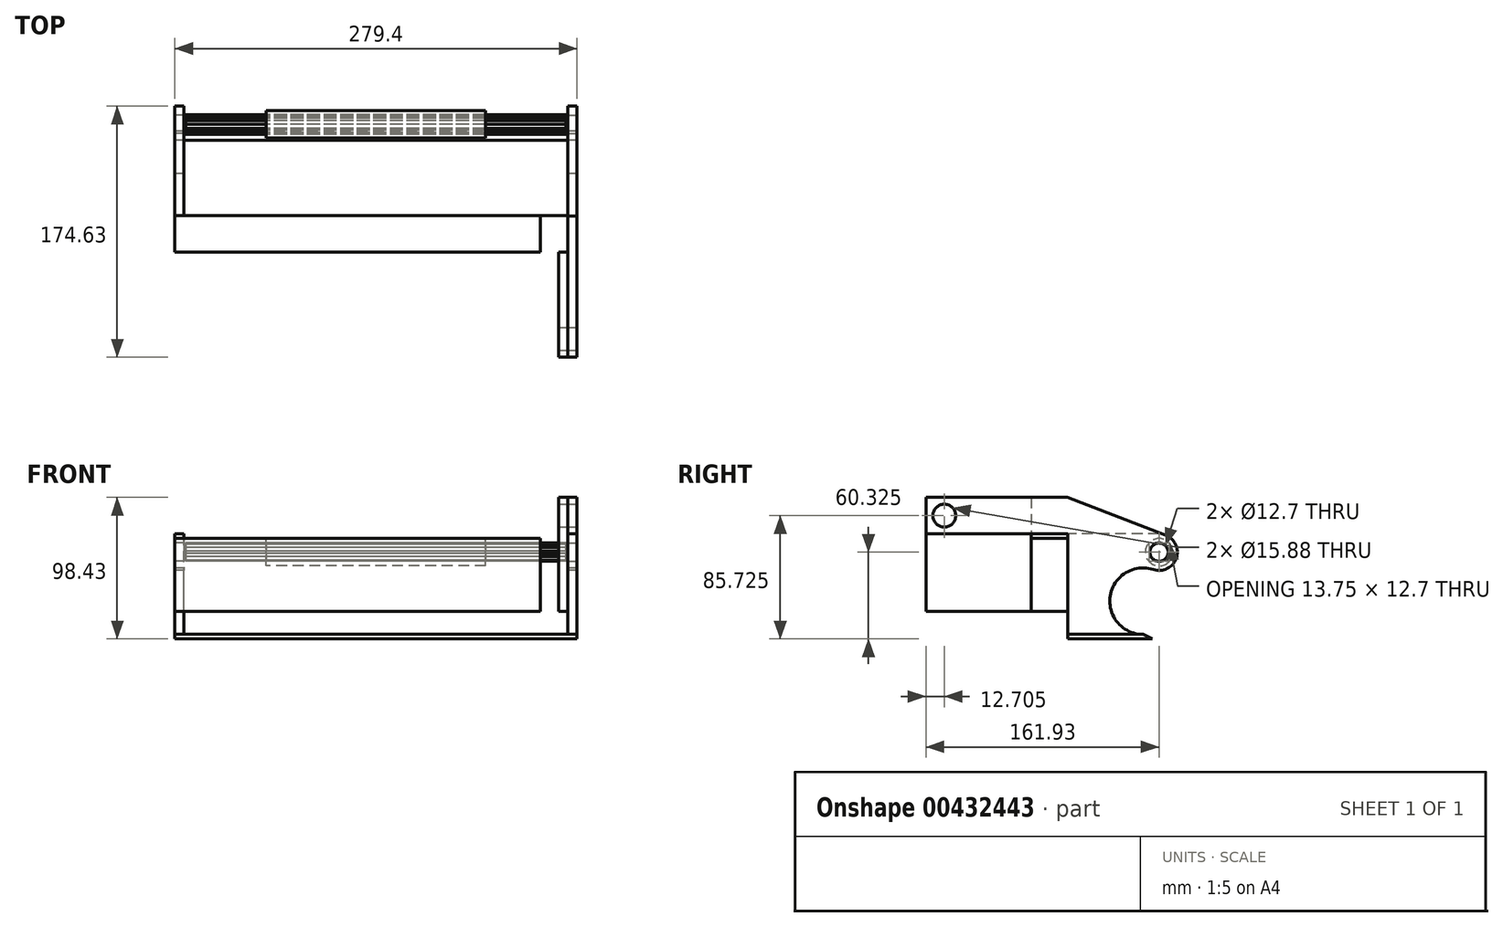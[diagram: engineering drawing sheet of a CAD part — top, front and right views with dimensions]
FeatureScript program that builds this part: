
annotation { "Feature Type Name" : "Feature", "Feature Type Description" : "" }
export const myFeature = defineFeature(function(context is Context, id is Id, definition is map)
    precondition{}
    {
        {
            var Q0;
            Q0=qCreatedBy(makeId("Right.planeOp"),FACE);
            var sketch = newSketch(context, id + "F0", { "sketchPlane" : qUnion([Q0])});
            skLineSegment(sketch, "E0.bottom", {"start": v(0, 19.05) * mm, "end": v(25.4, 19.05) * mm});
            skLineSegment(sketch, "E0.top", {"start": v(0, 69.85) * mm, "end": v(25.4, 69.85) * mm});
            skLineSegment(sketch, "E0.left", {"start": v(0, 19.05) * mm, "end": v(0, 69.85) * mm});
            skLineSegment(sketch, "E0.right", {"start": v(25.4, 19.05) * mm, "end": v(25.4, 69.85) * mm});
            skSolve(sketch);
        }
        {
            var Q0;
            Q0 = qSketchRegion(id + "F0", true);
            extrude(context, id + "F1", {"entities" : qUnion([Q0]), "depth" : 254 * mm});
        }
        {
            var Q0;
            Q0=qCreatedBy(makeId("Right.planeOp"),FACE);
            var sketch = newSketch(context, id + "F2", { "sketchPlane" : qUnion([Q0])});
            skLineSegment(sketch, "E1.bottom", {"start": v(25.4, 0) * mm, "end": v(84.14, 0) * mm});
            skLineSegment(sketch, "E1.top", {"start": v(25.4, 3.18) * mm, "end": v(77.79, 3.18) * mm});
            skLineSegment(sketch, "E1.left", {"start": v(25.4, 0) * mm, "end": v(25.4, 3.18) * mm});
            skLineSegment(sketch, "E2", {"start": v(84.14, 0) * mm, "end": v(77.79, 3.18) * mm});
            skSolve(sketch);
        }
        {
            var Q0;
            Q0 = qSketchRegion(id + "F2", true);
            extrude(context, id + "F3", {"entities" : qUnion([Q0]), "depth" : 279.4 * mm});
        }
        {
            var Q0;
            Q0=makeQuery(id+"F3.opExtrude","CAP_FACE",FACE,{"disambiguationData":[OSD([sQuery(id+"F2.wireOp",EDGE,"E1.bottom"),sQuery(id+"F2.wireOp",EDGE,"E1.top"),sQuery(id+"F2.wireOp",EDGE,"E1.left"),sQuery(id+"F2.wireOp",EDGE,"E2")])],"isStart":false});
            var Q1;
            Q1=makeQuery(id+"F3.opExtrude","CAP_FACE",FACE,{"disambiguationData":[OSD([sQuery(id+"F2.wireOp",EDGE,"E1.bottom"),sQuery(id+"F2.wireOp",EDGE,"E1.top"),sQuery(id+"F2.wireOp",EDGE,"E1.left"),sQuery(id+"F2.wireOp",EDGE,"E2")])],"isStart":true});
            cPlane(context, id + "F4", {"entities" : qUnion([Q0, Q1]), "cplaneType" : CPlaneType.MID_PLANE, "offset" : 25.4 * mm, "width" : 152.4 * mm, "height" : 152.4 * mm});
        }
        {
            var Q0;
            Q0=qCreatedBy(id+"F4.planeOp",FACE);
            var sketch = newSketch(context, id + "F5", { "sketchPlane" : qUnion([Q0])});
            skCircle(sketch, "E3.cCircle", {"center": v(88.9, 60.33) * mm, "radius": 6.35 * mm, "construction": true});
            skLineSegment(sketch, "E3.0", {"start": v(96.23, 60.33) * mm, "end": v(92.57, 53.98) * mm});
            skLineSegment(sketch, "E3.1", {"start": v(92.57, 53.98) * mm, "end": v(85.23, 53.98) * mm});
            skLineSegment(sketch, "E3.2", {"start": v(85.23, 53.97) * mm, "end": v(81.57, 60.32) * mm});
            skLineSegment(sketch, "E3.3", {"start": v(81.57, 60.32) * mm, "end": v(85.23, 66.68) * mm});
            skLineSegment(sketch, "E3.4", {"start": v(85.23, 66.68) * mm, "end": v(92.57, 66.68) * mm});
            skLineSegment(sketch, "E3.5", {"start": v(92.57, 66.68) * mm, "end": v(96.23, 60.33) * mm});
            skPoint(sketch, "E3.0.midPoint", {"position": v(94.4, 57.15) * mm});
            skCircle(sketch, "E4", {"center": v(88.9, 60.33) * mm, "radius": 6.88 * mm});
            skCircle(sketch, "E5", {"center": v(88.9, 60.33) * mm, "radius": 2.55 * mm});
            skSolve(sketch);
        }
        {
            var Q0;
            {var subQ0=sQuery(id+"F5.wireOp",EDGE,"E4");var subQ14=sQuery(id+"F5.wireOp",EDGE,"E3.0");var subQ15=makeQuery(id+"F5.imprint","INTERSECT",VERTEX,{"disambiguationData":[OD(0.0)],"derivedFrom":[subQ14,subQ0]});Q0=makeQuery(id+"F5.imprint","IMPRINT",FACE,{"disambiguationData":[TD([[makeQuery(id+"F5.imprint","IMPRINT",EDGE,{"disambiguationData":[TD([[subQ15,-1.0]])],"derivedFrom":subQ14}),-1.0]])]});}
            extrude(context, id + "F6", {"entities" : qUnion([Q0]), "depth" : 264.16 * mm, "symmetric" : true});
        }
        {
            var Q0;
            Q0=qCreatedBy(id+"F4.planeOp",FACE);
            var sketch = newSketch(context, id + "F7", { "sketchPlane" : qUnion([Q0])});
            skLineSegment(sketch, "E6.0.0", {"start": v(93.08, 65.78) * mm, "end": v(95.72, 61.22) * mm});
            skArc(sketch, "E6.0.1", {"start": v(95.72, 61.22) * mm, "mid": v(95.78, 60.33) * mm, "end": v(95.72, 59.43) * mm});
            skLineSegment(sketch, "E6.0.2", {"start": v(95.72, 59.43) * mm, "end": v(93.08, 54.87) * mm});
            skArc(sketch, "E6.0.3", {"start": v(93.08, 54.87) * mm, "mid": v(92.34, 54.37) * mm, "end": v(91.53, 53.97) * mm});
            skLineSegment(sketch, "E6.0.4", {"start": v(91.53, 53.98) * mm, "end": v(86.27, 53.98) * mm});
            skArc(sketch, "E6.0.5", {"start": v(86.27, 53.98) * mm, "mid": v(85.46, 54.37) * mm, "end": v(84.72, 54.87) * mm});
            skLineSegment(sketch, "E6.0.6", {"start": v(84.72, 54.87) * mm, "end": v(82.08, 59.43) * mm});
            skArc(sketch, "E6.0.7", {"start": v(82.08, 59.43) * mm, "mid": v(82.03, 60.32) * mm, "end": v(82.08, 61.22) * mm});
            skLineSegment(sketch, "E6.0.8", {"start": v(82.08, 61.22) * mm, "end": v(84.72, 65.78) * mm});
            skArc(sketch, "E6.0.9", {"start": v(84.72, 65.78) * mm, "mid": v(85.46, 66.28) * mm, "end": v(86.27, 66.68) * mm});
            skLineSegment(sketch, "E6.0.10", {"start": v(86.27, 66.68) * mm, "end": v(91.53, 66.68) * mm});
            skArc(sketch, "E6.0.11", {"start": v(91.53, 66.68) * mm, "mid": v(92.34, 66.28) * mm, "end": v(93.08, 65.78) * mm});
            skCircle(sketch, "E7", {"center": v(88.9, 60.33) * mm, "radius": 9.53 * mm});
            skSolve(sketch);
        }
        {
            var Q0;
            Q0 = qSketchRegion(id + "F7", true);
            extrude(context, id + "F8", {"entities" : qUnion([Q0]), "depth" : 152.4 * mm, "symmetric" : true});
        }
        {
            var Q0;
            Q0=makeQuery(id+"F3.opExtrude","CAP_FACE",FACE,{"disambiguationData":[OSD([sQuery(id+"F2.wireOp",EDGE,"E1.bottom"),sQuery(id+"F2.wireOp",EDGE,"E1.top"),sQuery(id+"F2.wireOp",EDGE,"E1.left"),sQuery(id+"F2.wireOp",EDGE,"E2")])],"isStart":true});
            var sketch = newSketch(context, id + "F9", { "sketchPlane" : qUnion([Q0])});
            skLineSegment(sketch, "E8.bottom", {"start": v(-101.6, 3.17) * mm, "end": v(-25.4, 3.17) * mm});
            skLineSegment(sketch, "E8.top", {"start": v(-101.6, 73.03) * mm, "end": v(-25.4, 73.03) * mm});
            skLineSegment(sketch, "E8.left", {"start": v(-101.6, 3.18) * mm, "end": v(-101.6, 73.03) * mm});
            skLineSegment(sketch, "E8.right", {"start": v(-25.4, 3.18) * mm, "end": v(-25.4, 73.03) * mm});
            skSolve(sketch);
        }
        {
            var Q0;
            Q0 = qSketchRegion(id + "F9", true);
            extrude(context, id + "F10", {"entities" : qUnion([Q0]), "oppositeDirection" : true, "depth" : 6.35 * mm});
        }
        {
            var Q0;
            Q0=makeQuery(id+"F10.opExtrude","CAP_FACE",FACE,{"disambiguationData":[OSD([sQuery(id+"F9.wireOp",EDGE,"E8.bottom"),sQuery(id+"F9.wireOp",EDGE,"E8.top"),sQuery(id+"F9.wireOp",EDGE,"E8.left"),sQuery(id+"F9.wireOp",EDGE,"E8.right")])],"isStart":true});
            var sketch = newSketch(context, id + "F11", { "sketchPlane" : qUnion([Q0])});
            skCircle(sketch, "E9", {"center": v(-88.9, 60.33) * mm, "radius": 6.35 * mm});
            skLineSegment(sketch, "E10.0.0", {"start": v(-93.08, 65.78) * mm, "end": v(-95.72, 61.22) * mm, "construction": true});
            skArc(sketch, "E10.0.1", {"start": v(-95.72, 61.22) * mm, "mid": v(-95.78, 60.33) * mm, "end": v(-95.72, 59.43) * mm, "construction": true});
            skLineSegment(sketch, "E10.0.2", {"start": v(-95.72, 59.43) * mm, "end": v(-93.08, 54.87) * mm, "construction": true});
            skArc(sketch, "E10.0.3", {"start": v(-93.08, 54.87) * mm, "mid": v(-92.34, 54.37) * mm, "end": v(-91.53, 53.97) * mm, "construction": true});
            skLineSegment(sketch, "E10.0.4", {"start": v(-91.53, 53.98) * mm, "end": v(-86.27, 53.98) * mm, "construction": true});
            skArc(sketch, "E10.0.5", {"start": v(-86.27, 53.98) * mm, "mid": v(-85.46, 54.37) * mm, "end": v(-84.72, 54.87) * mm, "construction": true});
            skLineSegment(sketch, "E10.0.6", {"start": v(-84.72, 54.87) * mm, "end": v(-82.08, 59.43) * mm, "construction": true});
            skArc(sketch, "E10.0.7", {"start": v(-82.08, 59.43) * mm, "mid": v(-82.03, 60.32) * mm, "end": v(-82.08, 61.22) * mm, "construction": true});
            skLineSegment(sketch, "E10.0.8", {"start": v(-82.08, 61.22) * mm, "end": v(-84.72, 65.78) * mm, "construction": true});
            skArc(sketch, "E10.0.9", {"start": v(-84.72, 65.78) * mm, "mid": v(-85.46, 66.28) * mm, "end": v(-86.27, 66.68) * mm, "construction": true});
            skLineSegment(sketch, "E10.0.10", {"start": v(-86.27, 66.68) * mm, "end": v(-91.53, 66.68) * mm, "construction": true});
            skArc(sketch, "E10.0.11", {"start": v(-91.53, 66.68) * mm, "mid": v(-92.34, 66.28) * mm, "end": v(-93.08, 65.78) * mm, "construction": true});
            skSolve(sketch);
        }
        {
            var Q0;
            Q0 = qSketchRegion(id + "F11", true);
            extrude(context, id + "F12", {"entities" : qUnion([Q0]), "operationType" : NewBodyOperationType.REMOVE, "endBound" : BoundingType.THROUGH_ALL, "oppositeDirection" : true, "depth" : 25.4 * mm});
        }
        {
            var Q0;
            Q0=makeQuery(id+"F6.opExtrude","CAP_FACE",FACE,{"disambiguationData":[OSD([sQuery(id+"F5.wireOp",EDGE,"E3.0"),sQuery(id+"F5.wireOp",EDGE,"E3.1"),sQuery(id+"F5.wireOp",EDGE,"E3.2"),sQuery(id+"F5.wireOp",EDGE,"E3.3"),sQuery(id+"F5.wireOp",EDGE,"E3.4"),sQuery(id+"F5.wireOp",EDGE,"E3.5"),sQuery(id+"F5.wireOp",EDGE,"E4"),sQuery(id+"F5.wireOp",EDGE,"E5")])],"isStart":true});
            var sketch = newSketch(context, id + "F13", { "sketchPlane" : qUnion([Q0])});
            skCircle(sketch, "E11", {"center": v(-88.9, 60.33) * mm, "radius": 3.18 * mm});
            skSolve(sketch);
        }
        {
            var Q0;
            Q0 = qSketchRegion(id + "F13", true);
            extrude(context, id + "F14", {"entities" : qUnion([Q0]), "oppositeDirection" : true, "depth" : 4.76 * mm});
        }
        {
            var Q0;
            Q0=makeQuery(id+"F14.opExtrude","SWEPT_BODY",BODY,{"disambiguationData":[OSD([sQuery(id+"F13.wireOp",EDGE,"E11")])]});
            var Q1;
            Q1=qCreatedBy(id+"F4.planeOp",FACE);
            mirror(context, id + "F15", {"operationType" : NewBodyOperationType.ADD, "entities" : qUnion([Q0]), "mirrorPlane" : qUnion([Q1])});
        }
        {
            var Q0;
            Q0=makeQuery(id+"F15.opPattern","COPY",BODY,{"derivedFrom":makeQuery(id+"F14.opExtrude","SWEPT_BODY",BODY,{"disambiguationData":[OSD([sQuery(id+"F13.wireOp",EDGE,"E11")])]}),"instanceName":"1"});
            var Q1;
            Q1=makeQuery(id+"F14.opExtrude","SWEPT_BODY",BODY,{"disambiguationData":[OSD([sQuery(id+"F13.wireOp",EDGE,"E11")])]});
            var Q2;
            Q2=makeQuery(id+"F6.opExtrude","SWEPT_BODY",BODY,{"disambiguationData":[OSD([sQuery(id+"F5.wireOp",EDGE,"E3.0"),sQuery(id+"F5.wireOp",EDGE,"E3.1"),sQuery(id+"F5.wireOp",EDGE,"E3.2"),sQuery(id+"F5.wireOp",EDGE,"E3.3"),sQuery(id+"F5.wireOp",EDGE,"E3.4"),sQuery(id+"F5.wireOp",EDGE,"E3.5"),sQuery(id+"F5.wireOp",EDGE,"E4"),sQuery(id+"F5.wireOp",EDGE,"E5")])]});
            booleanBodies(context, id + "F16", {"operationType" : BooleanOperationType.SUBTRACTION, "tools" : qUnion([Q0, Q1]), "targets" : qUnion([Q2])});
        }
        {
            var Q0;
            Q0=makeQuery(id+"F10.opExtrude","SWEPT_BODY",BODY,{"disambiguationData":[OSD([sQuery(id+"F9.wireOp",EDGE,"E8.bottom"),sQuery(id+"F9.wireOp",EDGE,"E8.top"),sQuery(id+"F9.wireOp",EDGE,"E8.left"),sQuery(id+"F9.wireOp",EDGE,"E8.right")])]});
            var Q1;
            Q1=qCreatedBy(id+"F4.planeOp",FACE);
            mirror(context, id + "F17", {"entities" : qUnion([Q0]), "mirrorPlane" : qUnion([Q1])});
        }
        {
            var Q0;
            Q0=makeQuery(id+"F10.opExtrude","CAP_FACE",FACE,{"disambiguationData":[OSD([sQuery(id+"F9.wireOp",EDGE,"E8.bottom"),sQuery(id+"F9.wireOp",EDGE,"E8.top"),sQuery(id+"F9.wireOp",EDGE,"E8.left"),sQuery(id+"F9.wireOp",EDGE,"E8.right")])],"isStart":true});
            var sketch = newSketch(context, id + "F18", { "sketchPlane" : qUnion([Q0])});
            skCircle(sketch, "E12", {"center": v(-88.9, 60.33) * mm, "radius": 12.7 * mm});
            skCircle(sketch, "E13", {"center": v(-77.79, 26.28) * mm, "radius": 23.1 * mm});
            skLineSegment(sketch, "E14.0", {"start": v(-25.4, 3.18) * mm, "end": v(-77.79, 3.18) * mm, "construction": true});
            skSolve(sketch);
        }
        {
            var Q0;
            {var subQ0=sQuery(id+"F18.wireOp",EDGE,"E12");var subQ1=makeQuery(id+"F10.opExtrude","CAP_EDGE",EDGE,{"disambiguationData":[OSD([sQuery(id+"F9.wireOp",EDGE,"E8.left")])],"isStart":true});var subQ2=makeQuery(id+"F18.imprint","INTERSECT",VERTEX,{"derivedFrom":[subQ1,subQ0]});Q0=makeQuery(id+"F18.imprint","IMPRINT",FACE,{"disambiguationData":[TD([[makeQuery(id+"F18.imprint","IMPRINT",EDGE,{"disambiguationData":[TD([[subQ2,1.0]])],"derivedFrom":subQ0}),-1.0]])]});}
            var Q1;
            {var subQ0=sQuery(id+"F18.wireOp",EDGE,"E13");var subQ1=sQuery(id+"F18.wireOp",EDGE,"E12");var subQ2=makeQuery(id+"F18.imprint","INTERSECT",VERTEX,{"derivedFrom":[subQ1,subQ0]});Q1=makeQuery(id+"F18.imprint","IMPRINT",FACE,{"disambiguationData":[TD([[makeQuery(id+"F18.imprint","IMPRINT",EDGE,{"disambiguationData":[TD([[subQ2,1.0]])],"derivedFrom":subQ1}),-1.0]])]});}
            var Q2;
            {var subQ0=sQuery(id+"F18.wireOp",EDGE,"E13");var subQ1=makeQuery(id+"F18.imprint","INTERSECT",VERTEX,{"derivedFrom":[sQuery(id+"F18.wireOp",EDGE,"E12"),subQ0]});Q2=makeQuery(id+"F18.imprint","IMPRINT",FACE,{"disambiguationData":[TD([[makeQuery(id+"F18.imprint","IMPRINT",EDGE,{"disambiguationData":[TD([[subQ1,-1.0]])],"derivedFrom":subQ0}),1.0]])]});}
            var Q3;
            {var subQ0=sQuery(id+"F18.wireOp",EDGE,"E13");var subQ1=makeQuery(id+"F10.opExtrude","CAP_EDGE",EDGE,{"disambiguationData":[OSD([sQuery(id+"F9.wireOp",EDGE,"E8.left")])],"isStart":true});var subQ2=makeQuery(id+"F18.imprint","INTERSECT",VERTEX,{"disambiguationData":[OD(1.0)],"derivedFrom":[subQ1,subQ0]});Q3=makeQuery(id+"F18.imprint","IMPRINT",FACE,{"disambiguationData":[TD([[makeQuery(id+"F18.imprint","IMPRINT",EDGE,{"disambiguationData":[TD([[subQ2,-1.0]])],"derivedFrom":subQ0}),-1.0]])]});}
            extrude(context, id + "F19", {"entities" : qUnion([Q0, Q1, Q2, Q3]), "operationType" : NewBodyOperationType.REMOVE, "endBound" : BoundingType.THROUGH_ALL, "oppositeDirection" : true, "depth" : 25.4 * mm});
        }
        {
            var Q0;
            Q0=makeQuery(id+"F17.opPattern","COPY",FACE,{"derivedFrom":makeQuery(id+"F10.opExtrude","CAP_FACE",FACE,{"disambiguationData":[OSD([sQuery(id+"F9.wireOp",EDGE,"E8.bottom"),sQuery(id+"F9.wireOp",EDGE,"E8.top"),sQuery(id+"F9.wireOp",EDGE,"E8.left"),sQuery(id+"F9.wireOp",EDGE,"E8.right")])],"isStart":true}),"instanceName":"1"});
            var sketch = newSketch(context, id + "F20", { "sketchPlane" : qUnion([Q0])});
            skLineSegment(sketch, "E15.bottom", {"start": v(-73.03, 98.43) * mm, "end": v(101.44, 98.43) * mm});
            skLineSegment(sketch, "E15.top", {"start": v(-73.03, 73.03) * mm, "end": v(101.44, 73.03) * mm});
            skLineSegment(sketch, "E15.left", {"start": v(-73.03, 98.43) * mm, "end": v(-73.03, 73.03) * mm});
            skLineSegment(sketch, "E15.right", {"start": v(101.44, 98.43) * mm, "end": v(101.44, 73.03) * mm});
            skArc(sketch, "E16.0", {"start": v(84.96, 48.25) * mm, "mid": v(101.44, 58.33) * mm, "end": v(88.9, 73.03) * mm});
            skLineSegment(sketch, "E17", {"start": v(101.44, 73.03) * mm, "end": v(101.44, 58.33) * mm});
            skPoint(sketch, "E17.endSnap0", {"position": v(101.44, 58.33) * mm});
            skSolve(sketch);
        }
        {
            var Q0;
            Q0 = qSketchRegion(id + "F20", true);
            var Q1;
            Q1=makeQuery(id+"F17.opPattern","COPY",FACE,{"derivedFrom":makeQuery(id+"F10.opExtrude","CAP_FACE",FACE,{"disambiguationData":[OSD([sQuery(id+"F9.wireOp",EDGE,"E8.bottom"),sQuery(id+"F9.wireOp",EDGE,"E8.top"),sQuery(id+"F9.wireOp",EDGE,"E8.left"),sQuery(id+"F9.wireOp",EDGE,"E8.right")])],"isStart":false}),"instanceName":"1"});
            extrude(context, id + "F21", {"entities" : qUnion([Q0]), "operationType" : NewBodyOperationType.ADD, "endBound" : BoundingType.UP_TO_SURFACE, "oppositeDirection" : true, "endBoundEntityFace" : qUnion([Q1]), "depth" : 25.4 * mm});
        }
        {
            var Q0;
            Q0=makeQuery(id+"F21.boolean.opBoolean","MERGE",FACE,{"derivedFrom":[makeQuery(id+"F17.opPattern","COPY",FACE,{"derivedFrom":makeQuery(id+"F10.opExtrude","CAP_FACE",FACE,{"disambiguationData":[OSD([sQuery(id+"F9.wireOp",EDGE,"E8.bottom"),sQuery(id+"F9.wireOp",EDGE,"E8.top"),sQuery(id+"F9.wireOp",EDGE,"E8.left"),sQuery(id+"F9.wireOp",EDGE,"E8.right")])],"isStart":true}),"instanceName":"1"}),makeQuery(id+"F21.opExtrude","CAP_FACE",FACE,{"disambiguationData":[OSD([sQuery(id+"F20.wireOp",EDGE,"E15.bottom"),sQuery(id+"F20.wireOp",EDGE,"E15.top"),sQuery(id+"F20.wireOp",EDGE,"E15.left"),sQuery(id+"F20.wireOp",EDGE,"E15.right")])],"isStart":true})]});
            var sketch = newSketch(context, id + "F22", { "sketchPlane" : qUnion([Q0])});
            skCircle(sketch, "E18", {"center": v(-60.33, 85.73) * mm, "radius": 7.94 * mm});
            skLineSegment(sketch, "E19", {"start": v(-73.03, 85.72) * mm, "end": v(-60.33, 85.72) * mm, "construction": true});
            skCircle(sketch, "E20", {"center": v(88.9, 60.33) * mm, "radius": 12.7 * mm});
            skLineSegment(sketch, "E21", {"start": v(93.46, 72.18) * mm, "end": v(25.24, 98.43) * mm});
            skLineSegment(sketch, "E22", {"start": v(25.24, 98.43) * mm, "end": v(101.44, 98.43) * mm});
            skLineSegment(sketch, "E23", {"start": v(101.44, 98.43) * mm, "end": v(101.6, 60.38) * mm});
            skSolve(sketch);
        }
        {
            var Q0;
            Q0=makeQuery(id+"F22.imprint","IMPRINT",FACE,{"disambiguationData":[TD([[makeQuery(id+"F22.imprint","IMPRINT",EDGE,{"derivedFrom":sQuery(id+"F22.wireOp",EDGE,"E18")}),1.0]])]});
            var Q1;
            {var subQ2=sQuery(id+"F22.wireOp",EDGE,"E21");Q1=makeQuery(id+"F22.imprint","IMPRINT",FACE,{"disambiguationData":[TD([[makeQuery(id+"F22.imprint","IMPRINT",EDGE,{"derivedFrom":subQ2}),-1.0]])]});}
            extrude(context, id + "F23", {"entities" : qUnion([Q0, Q1]), "operationType" : NewBodyOperationType.REMOVE, "endBound" : BoundingType.THROUGH_ALL, "oppositeDirection" : true, "depth" : 25.4 * mm});
        }
        {
            var Q0;
            {var subQ0=sQuery(id+"F9.wireOp",EDGE,"E8.right");var subQ1=sQuery(id+"F9.wireOp",EDGE,"E8.left");var subQ2=sQuery(id+"F9.wireOp",EDGE,"E8.top");var subQ3=sQuery(id+"F9.wireOp",EDGE,"E8.bottom");Q0=makeQuery(id+"F21.boolean.opBoolean","MERGE",FACE,{"derivedFrom":[makeQuery(id+"F17.opPattern","COPY",FACE,{"derivedFrom":makeQuery(id+"F10.opExtrude","CAP_FACE",FACE,{"disambiguationData":[OSD([subQ3,subQ2,subQ1,subQ0])],"isStart":false}),"instanceName":"1"}),makeQuery(id+"F21.opExtrude","CAP_FACE",FACE,{"disambiguationData":[OSD([subQ3,subQ2,subQ1,subQ0]),ownerDisambiguation([makeQuery(id+"F20.imprint","IMPRINT",EDGE,{"derivedFrom":sQuery(id+"F20.wireOp",EDGE,"E15.bottom")})])],"isStart":false})]});}
            var sketch = newSketch(context, id + "F24", { "sketchPlane" : qUnion([Q0])});
            skCircle(sketch, "E24.0", {"center": v(60.33, 85.73) * mm, "radius": 7.94 * mm});
            skLineSegment(sketch, "E25.0", {"start": v(0, 19.05) * mm, "end": v(0, 69.85) * mm});
            skLineSegment(sketch, "E26", {"start": v(0, 19.05) * mm, "end": v(73.03, 19.05) * mm});
            skLineSegment(sketch, "E27", {"start": v(73.03, 19.05) * mm, "end": v(73.03, 98.43) * mm});
            skLineSegment(sketch, "E28", {"start": v(73.03, 98.43) * mm, "end": v(0, 98.43) * mm});
            skLineSegment(sketch, "E29", {"start": v(0, 98.43) * mm, "end": v(0, 69.85) * mm});
            skSolve(sketch);
        }
        {
            var Q0;
            Q0 = qSketchRegion(id + "F24", true);
            extrude(context, id + "F25", {"entities" : qUnion([Q0]), "depth" : 6.35 * mm});
        }
    });
